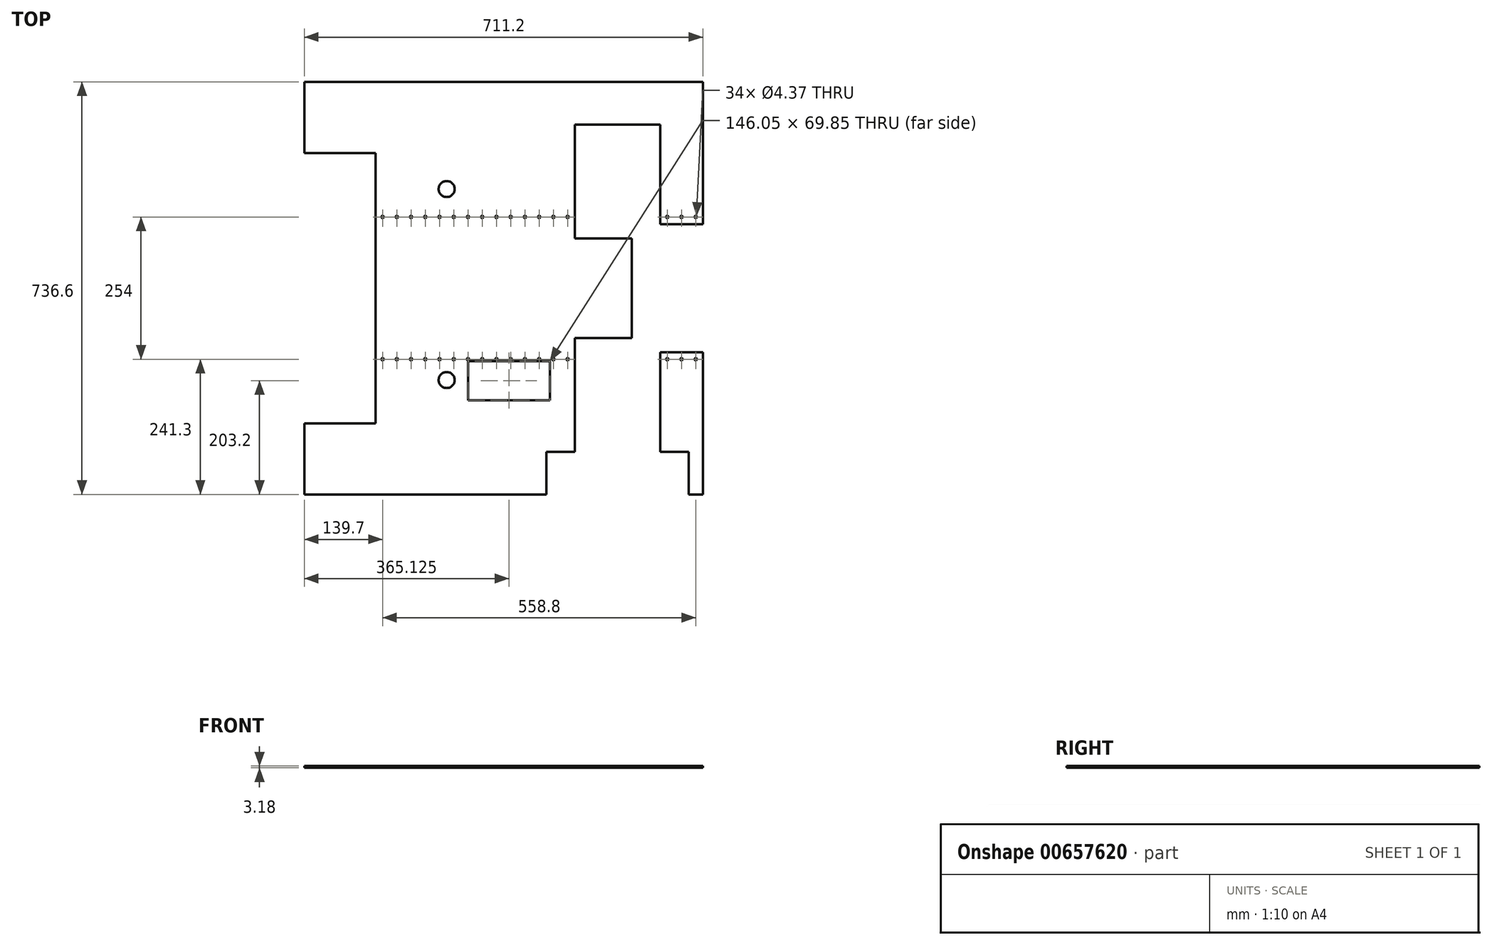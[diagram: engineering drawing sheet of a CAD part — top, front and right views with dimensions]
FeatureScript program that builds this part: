
annotation { "Feature Type Name" : "Feature", "Feature Type Description" : "" }
export const myFeature = defineFeature(function(context is Context, id is Id, definition is map)
    precondition{}
    {
        {
            var Q0;
            Q0=qCreatedBy(makeId("Top.planeOp"),FACE);
            var sketch = newSketch(context, id + "F0", { "sketchPlane" : qUnion([Q0])});
            skLineSegment(sketch, "E0.bottom", {"start": v(0, 0) * mm, "end": v(711.2, 0) * mm});
            skLineSegment(sketch, "E0.top", {"start": v(0, -736.6) * mm, "end": v(711.2, -736.6) * mm});
            skLineSegment(sketch, "E0.left", {"start": v(0, 0) * mm, "end": v(0, -736.6) * mm});
            skLineSegment(sketch, "E0.right", {"start": v(711.2, 0) * mm, "end": v(711.2, -736.6) * mm});
            skCircle(sketch, "E1", {"center": v(114.3, -241.3) * mm, "radius": 2.18 * mm});
            skCircle(sketch, "E2.0.1.0", {"center": v(114.3, -495.3) * mm, "radius": 2.18 * mm});
            skCircle(sketch, "E3.1.0.0", {"center": v(139.7, -241.3) * mm, "radius": 2.18 * mm});
            skCircle(sketch, "E3.2.0.0", {"center": v(165.1, -241.3) * mm, "radius": 2.18 * mm});
            skCircle(sketch, "E3.3.0.0", {"center": v(190.5, -241.3) * mm, "radius": 2.18 * mm});
            skCircle(sketch, "E3.4.0.0", {"center": v(215.9, -241.3) * mm, "radius": 2.18 * mm});
            skCircle(sketch, "E3.5.0.0", {"center": v(241.3, -241.3) * mm, "radius": 2.18 * mm});
            skCircle(sketch, "E3.6.0.0", {"center": v(266.7, -241.3) * mm, "radius": 2.18 * mm});
            skCircle(sketch, "E3.7.0.0", {"center": v(292.1, -241.3) * mm, "radius": 2.18 * mm});
            skCircle(sketch, "E3.8.0.0", {"center": v(317.5, -241.3) * mm, "radius": 2.18 * mm});
            skCircle(sketch, "E3.9.0.0", {"center": v(342.9, -241.3) * mm, "radius": 2.18 * mm});
            skCircle(sketch, "E3.10.0.0", {"center": v(368.3, -241.3) * mm, "radius": 2.18 * mm});
            skCircle(sketch, "E3.11.0.0", {"center": v(393.7, -241.3) * mm, "radius": 2.18 * mm});
            skCircle(sketch, "E3.12.0.0", {"center": v(419.1, -241.3) * mm, "radius": 2.18 * mm});
            skCircle(sketch, "E3.13.0.0", {"center": v(444.5, -241.3) * mm, "radius": 2.18 * mm});
            skCircle(sketch, "E3.14.0.0", {"center": v(469.9, -241.3) * mm, "radius": 2.18 * mm});
            skCircle(sketch, "E3.15.0.0", {"center": v(495.3, -241.3) * mm, "radius": 2.18 * mm});
            skCircle(sketch, "E3.16.0.0", {"center": v(520.7, -241.3) * mm, "radius": 2.18 * mm});
            skCircle(sketch, "E3.17.0.0", {"center": v(546.1, -241.3) * mm, "radius": 2.18 * mm});
            skCircle(sketch, "E3.18.0.0", {"center": v(571.5, -241.3) * mm, "radius": 2.18 * mm});
            skCircle(sketch, "E3.19.0.0", {"center": v(596.9, -241.3) * mm, "radius": 2.18 * mm});
            skLineSegment(sketch, "E3.direction1", {"start": v(139.7, -241.3) * mm, "end": v(114.3, -241.3) * mm, "construction": true});
            skCircle(sketch, "E4.0.20.0", {"center": v(622.3, -241.3) * mm, "radius": 2.18 * mm});
            skCircle(sketch, "E4.0.21.0", {"center": v(647.7, -241.3) * mm, "radius": 2.18 * mm});
            skCircle(sketch, "E4.0.22.0", {"center": v(673.1, -241.3) * mm, "radius": 2.18 * mm});
            skCircle(sketch, "E4.0.23.0", {"center": v(698.5, -241.3) * mm, "radius": 2.18 * mm});
            skLineSegment(sketch, "E5.direction1", {"start": v(698.5, -241.3) * mm, "end": v(723.9, -241.3) * mm, "construction": true});
            skCircle(sketch, "E6.1.0.0", {"center": v(139.7, -495.3) * mm, "radius": 2.18 * mm});
            skCircle(sketch, "E6.2.0.0", {"center": v(165.1, -495.3) * mm, "radius": 2.18 * mm});
            skCircle(sketch, "E6.3.0.0", {"center": v(190.5, -495.3) * mm, "radius": 2.18 * mm});
            skCircle(sketch, "E6.4.0.0", {"center": v(215.9, -495.3) * mm, "radius": 2.18 * mm});
            skCircle(sketch, "E6.5.0.0", {"center": v(241.3, -495.3) * mm, "radius": 2.18 * mm});
            skCircle(sketch, "E6.6.0.0", {"center": v(266.7, -495.3) * mm, "radius": 2.18 * mm});
            skCircle(sketch, "E6.7.0.0", {"center": v(292.1, -495.3) * mm, "radius": 2.18 * mm});
            skCircle(sketch, "E6.8.0.0", {"center": v(317.5, -495.3) * mm, "radius": 2.18 * mm});
            skCircle(sketch, "E6.9.0.0", {"center": v(342.9, -495.3) * mm, "radius": 2.18 * mm});
            skCircle(sketch, "E6.10.0.0", {"center": v(368.3, -495.3) * mm, "radius": 2.18 * mm});
            skCircle(sketch, "E6.11.0.0", {"center": v(393.7, -495.3) * mm, "radius": 2.18 * mm});
            skCircle(sketch, "E6.12.0.0", {"center": v(419.1, -495.3) * mm, "radius": 2.18 * mm});
            skCircle(sketch, "E6.13.0.0", {"center": v(444.5, -495.3) * mm, "radius": 2.18 * mm});
            skCircle(sketch, "E6.14.0.0", {"center": v(469.9, -495.3) * mm, "radius": 2.18 * mm});
            skCircle(sketch, "E6.15.0.0", {"center": v(495.3, -495.3) * mm, "radius": 2.18 * mm});
            skCircle(sketch, "E6.16.0.0", {"center": v(520.7, -495.3) * mm, "radius": 2.18 * mm});
            skCircle(sketch, "E6.17.0.0", {"center": v(546.1, -495.3) * mm, "radius": 2.18 * mm});
            skCircle(sketch, "E6.18.0.0", {"center": v(571.5, -495.3) * mm, "radius": 2.18 * mm});
            skCircle(sketch, "E6.19.0.0", {"center": v(596.9, -495.3) * mm, "radius": 2.18 * mm});
            skCircle(sketch, "E6.20.0.0", {"center": v(622.3, -495.3) * mm, "radius": 2.18 * mm});
            skCircle(sketch, "E6.21.0.0", {"center": v(647.7, -495.3) * mm, "radius": 2.18 * mm});
            skCircle(sketch, "E6.22.0.0", {"center": v(673.1, -495.3) * mm, "radius": 2.18 * mm});
            skCircle(sketch, "E6.23.0.0", {"center": v(698.5, -495.3) * mm, "radius": 2.18 * mm});
            skLineSegment(sketch, "E6.direction1", {"start": v(114.3, -495.3) * mm, "end": v(139.7, -495.3) * mm, "construction": true});
            skLineSegment(sketch, "E7.bottom", {"start": v(711.2, -254) * mm, "end": v(584.2, -254) * mm});
            skLineSegment(sketch, "E7.top", {"start": v(711.2, -482.6) * mm, "end": v(584.2, -482.6) * mm});
            skLineSegment(sketch, "E7.left", {"start": v(711.2, -254) * mm, "end": v(711.2, -482.6) * mm});
            skLineSegment(sketch, "E7.right", {"start": v(584.2, -254) * mm, "end": v(584.2, -482.6) * mm});
            skCircle(sketch, "E8", {"center": v(254, -191.45) * mm, "radius": 14.29 * mm});
            skCircle(sketch, "E9", {"center": v(254, -532.45) * mm, "radius": 14.29 * mm});
            skLineSegment(sketch, "E10.bottom", {"start": v(584.2, -366.71) * mm, "end": v(387.35, -366.71) * mm});
            skLineSegment(sketch, "E10.top", {"start": v(584.2, -357.19) * mm, "end": v(387.35, -357.19) * mm});
            skLineSegment(sketch, "E10.left", {"start": v(584.2, -357.19) * mm, "end": v(584.2, -366.71) * mm});
            skLineSegment(sketch, "E10.right", {"start": v(387.35, -357.19) * mm, "end": v(387.35, -366.71) * mm});
            skLineSegment(sketch, "E11.left", {"start": v(584.2, -225.43) * mm, "end": v(584.2, -228.6) * mm});
            skLineSegment(sketch, "E11.right", {"start": v(387.35, -225.43) * mm, "end": v(387.35, -228.6) * mm});
            skLineSegment(sketch, "E12.left", {"start": v(584.2, -495.3) * mm, "end": v(584.2, -498.47) * mm});
            skLineSegment(sketch, "E12.right", {"start": v(387.35, -495.3) * mm, "end": v(387.35, -498.48) * mm});
            skLineSegment(sketch, "E13.right", {"start": v(387.35, -498.48) * mm, "end": v(387.35, -523.88) * mm});
            skLineSegment(sketch, "E14.bottom", {"start": v(438.15, -498.48) * mm, "end": v(292.1, -498.48) * mm});
            skLineSegment(sketch, "E14.top", {"start": v(438.15, -568.32) * mm, "end": v(292.1, -568.32) * mm});
            skLineSegment(sketch, "E14.left", {"start": v(438.15, -498.48) * mm, "end": v(438.15, -568.32) * mm});
            skLineSegment(sketch, "E14.right", {"start": v(292.1, -498.48) * mm, "end": v(292.1, -568.32) * mm});
            skLineSegment(sketch, "E15.bottom", {"start": v(0, -609.6) * mm, "end": v(127, -609.6) * mm});
            skLineSegment(sketch, "E15.top", {"start": v(0, -127) * mm, "end": v(127, -127) * mm});
            skLineSegment(sketch, "E15.left", {"start": v(0, -609.6) * mm, "end": v(0, -127) * mm});
            skLineSegment(sketch, "E15.right", {"start": v(127, -609.6) * mm, "end": v(127, -127) * mm});
            skLineSegment(sketch, "E16.bottom", {"start": v(711.2, -736.6) * mm, "end": v(685.8, -736.6) * mm});
            skLineSegment(sketch, "E16.top", {"start": v(711.2, -482.6) * mm, "end": v(685.8, -482.6) * mm});
            skLineSegment(sketch, "E16.left", {"start": v(711.2, -736.6) * mm, "end": v(711.2, -482.6) * mm});
            skLineSegment(sketch, "E16.right", {"start": v(685.8, -736.6) * mm, "end": v(685.8, -482.6) * mm});
            skLineSegment(sketch, "E17.bottom", {"start": v(685.8, -736.6) * mm, "end": v(431.8, -736.6) * mm});
            skLineSegment(sketch, "E17.top", {"start": v(685.8, -660.4) * mm, "end": v(431.8, -660.4) * mm});
            skLineSegment(sketch, "E17.left", {"start": v(685.8, -736.6) * mm, "end": v(685.8, -660.4) * mm});
            skLineSegment(sketch, "E17.right", {"start": v(431.8, -736.6) * mm, "end": v(431.8, -660.4) * mm});
            skLineSegment(sketch, "E18.bottom", {"start": v(635, -660.4) * mm, "end": v(482.6, -660.4) * mm});
            skLineSegment(sketch, "E18.top", {"start": v(635, -457.2) * mm, "end": v(482.6, -457.2) * mm});
            skLineSegment(sketch, "E18.left", {"start": v(635, -660.4) * mm, "end": v(635, -457.2) * mm});
            skLineSegment(sketch, "E18.right", {"start": v(482.6, -660.4) * mm, "end": v(482.6, -457.2) * mm});
            skLineSegment(sketch, "E19.bottom", {"start": v(711.2, -254) * mm, "end": v(685.8, -254) * mm});
            skLineSegment(sketch, "E19.top", {"start": v(711.2, 0) * mm, "end": v(685.8, 0) * mm});
            skLineSegment(sketch, "E19.left", {"start": v(711.2, -254) * mm, "end": v(711.2, 0) * mm});
            skLineSegment(sketch, "E19.right", {"start": v(685.8, -254) * mm, "end": v(685.8, 0) * mm});
            skLineSegment(sketch, "E20.bottom", {"start": v(685.8, 0) * mm, "end": v(431.8, 0) * mm});
            skLineSegment(sketch, "E20.top", {"start": v(685.8, -76.2) * mm, "end": v(431.8, -76.2) * mm});
            skLineSegment(sketch, "E20.left", {"start": v(685.8, 0) * mm, "end": v(685.8, -76.2) * mm});
            skLineSegment(sketch, "E20.right", {"start": v(431.8, 0) * mm, "end": v(431.8, -76.2) * mm});
            skLineSegment(sketch, "E21.bottom", {"start": v(482.6, -76.2) * mm, "end": v(635, -76.2) * mm});
            skLineSegment(sketch, "E21.top", {"start": v(482.6, -279.4) * mm, "end": v(635, -279.4) * mm});
            skLineSegment(sketch, "E21.left", {"start": v(482.6, -76.2) * mm, "end": v(482.6, -279.4) * mm});
            skLineSegment(sketch, "E21.right", {"start": v(635, -76.2) * mm, "end": v(635, -279.4) * mm});
            skSolve(sketch);
        }
        {
            var Q0;
            Q0=makeQuery(id+"F0.imprint","IMPRINT",FACE,{"disambiguationData":[TD([[makeQuery(id+"F0.imprint","IMPRINT",EDGE,{"derivedFrom":sQuery(id+"F0.wireOp",EDGE,"GHKAK88V-Qg7s-zwJT-1rFb-I82lPg0xsoRr.bottom")}),-1.0]])]});
            var Q1;
            Q1=makeQuery(id+"F0.imprint","IMPRINT",FACE,{"disambiguationData":[TD([[makeQuery(id+"F0.imprint","IMPRINT",EDGE,{"derivedFrom":sQuery(id+"F0.wireOp",EDGE,"E9")}),-1.0]])]});
            var Q2;
            {var subQ0=sQuery(id+"F0.wireOp",EDGE,"E13.right");Q2=makeQuery(id+"F0.imprint","IMPRINT",FACE,{"disambiguationData":[TD([[makeQuery(id+"F0.imprint","IMPRINT",EDGE,{"derivedFrom":subQ0}),1.0]])]});}
            var Q3;
            Q3=makeQuery(id+"F0.imprint","IMPRINT",FACE,{"disambiguationData":[TD([[makeQuery(id+"F0.imprint","IMPRINT",EDGE,{"derivedFrom":sQuery(id+"F0.wireOp",EDGE,"E12.bottom")}),1.0]])]});
            var Q4;
            Q4=makeQuery(id+"F0.imprint","IMPRINT",FACE,{"disambiguationData":[TD([[makeQuery(id+"F0.imprint","IMPRINT",EDGE,{"derivedFrom":sQuery(id+"F0.wireOp",EDGE,"E11.bottom")}),1.0]])]});
            var Q5;
            Q5=makeQuery(id+"F0.imprint","IMPRINT",FACE,{"disambiguationData":[TD([[makeQuery(id+"F0.imprint","IMPRINT",EDGE,{"derivedFrom":sQuery(id+"F0.wireOp",EDGE,"E17.bottom")}),-1.0]])]});
            var Q6;
            Q6=makeQuery(id+"F0.imprint","IMPRINT",FACE,{"disambiguationData":[TD([[makeQuery(id+"F0.imprint","IMPRINT",EDGE,{"derivedFrom":sQuery(id+"F0.wireOp",EDGE,"E16.bottom")}),-1.0]])]});
            var Q7;
            {var subQ5=sQuery(id+"F0.wireOp",EDGE,"E13.bottom");var subQ6=makeQuery(id+"F0.imprint","INTERSECT",VERTEX,{"derivedFrom":[sQuery(id+"F0.wireOp",EDGE,"E12.right"),subQ5]});Q7=makeQuery(id+"F0.imprint","IMPRINT",FACE,{"disambiguationData":[TD([[makeQuery(id+"F0.imprint","IMPRINT",EDGE,{"disambiguationData":[TD([[subQ6,1.0]])],"derivedFrom":subQ5}),1.0]])]});}
            var Q8;
            {var subQ0=sQuery(id+"F0.wireOp",EDGE,"E0.bottom");Q8=makeQuery(id+"F0.imprint","IMPRINT",FACE,{"disambiguationData":[TD([[makeQuery(id+"F0.imprint","IMPRINT",EDGE,{"derivedFrom":subQ0}),-1.0]])]});}
            var Q9;
            Q9=makeQuery(id+"F0.imprint","IMPRINT",FACE,{"disambiguationData":[TD([[makeQuery(id+"F0.imprint","IMPRINT",EDGE,{"derivedFrom":sQuery(id+"F0.wireOp",EDGE,"E10.bottom")}),-1.0]])]});
            var Q10;
            Q10=makeQuery(id+"F0.imprint","IMPRINT",FACE,{"disambiguationData":[TD([[makeQuery(id+"F0.imprint","IMPRINT",EDGE,{"derivedFrom":sQuery(id+"F0.wireOp",EDGE,"E20.bottom")}),1.0]])]});
            var Q11;
            Q11=makeQuery(id+"F0.imprint","IMPRINT",FACE,{"disambiguationData":[TD([[makeQuery(id+"F0.imprint","IMPRINT",EDGE,{"derivedFrom":sQuery(id+"F0.wireOp",EDGE,"E19.bottom")}),-1.0]])]});
            var Q12;
            Q12=makeQuery(id+"F0.imprint","IMPRINT",FACE,{"disambiguationData":[TD([[makeQuery(id+"F0.imprint","IMPRINT",EDGE,{"derivedFrom":sQuery(id+"F0.wireOp",EDGE,"E7.top")}),1.0]])]});
            var Q13;
            Q13=makeQuery(id+"F0.imprint","IMPRINT",FACE,{"disambiguationData":[TD([[makeQuery(id+"F0.imprint","IMPRINT",EDGE,{"derivedFrom":sQuery(id+"F0.wireOp",EDGE,"E7.bottom")}),-1.0]])]});
            extrude(context, id + "F1", {"entities" : qUnion([Q0, Q1, Q2, Q3, Q4, Q5, Q6, Q7, Q8, Q9, Q10, Q11, Q12, Q13]), "depth" : 3.17 * mm, "offsetDistance" : 25.4 * mm});
        }
    });
